# Revit family: HDL106NE
name_source: partatom
category: Lighting Fixtures
revit_build: Autodesk Revit 2014 (Build: 20130308_1515(x64)
units: mm (PartAtom-declared; Revit-internal decimal feet)

## types (1)
- HDL106NE
    Apparent Load = 65 VA
    Assembly Code = D5020200
    Color Filter = 16777215
    Connector Description = Lighting Connector
    Default Elevation = 1219.2 mm  [stored 4 ft]
    Description = The HDL106NE is a distinctive Emergency LED luminaire allowing
up to three modules interlinked, providing an effective and efficient
alternative to traditional battery-backed luminaires.
With a variety of beam options available, and integral battery backup
allowing for either 90 minutes or 3 hours battery duration, this is a
flexible solution for any Emergency or Escape to Sea application.
    Dimming Lamp Color Temperature Shift = <None>
    Emit Shape Visible in Rendering = No
    Emit from Rectangle Length = 180 mm  [stored 0.590551 ft]
    Emit from Rectangle Width = 250 mm  [stored 0.82021 ft]
    Features = Instant on crisp white light output 80,000 maintenance free hours at 25°
Highly Energy Efficient Lower power consumption than HID lamps
Modular design allowing up to three interlinked
luminaires, each providing a delivered output > 5500lm Lightweight (9kg per module) lighting solution
>150,000 maintenance free hours at 25°C (L70)
    Fixture distribution = Direct
    Glass = Hubbell - Glass
    Height = 535 mm
    Housing Material = Paint - Hubbell - Light Silver
    IP Rating = IP66/67
    Lamp = LED
    Length = 265 mm  [stored 0.869423 ft]
    Load Classification = Lighting
    Manufacturer = Chalmit
    Model = HDL106NE
    Mounting = Paint - Hubbell - Light Silver
    Photometric Web File = HDL106NEEEMWx04.ies
    Power Factor = 1
    Product Documentation Link = https://hubbellcdn.com
    Product Link = https://www.hubbell.com
    Reflector Finish = Hubbell - White Glass
    Tilt Angle = 90.00°
    URL = https://www.hubbell.com
    Voltage = 120 V
    Warranty = 5 years Warranty
    Wattage Comments = 65W
    Watts = 65 W
    Width = 280 mm
    Wings = Paint - Hubbell - Light Silver

note: [stored X ft] marks values corroborated as IEEE doubles in the binary element streams (Revit-internal decimal feet)

## geometry (parser evidence)
native form markers: Sweep x4
no freeform markers — native parametric forms only
